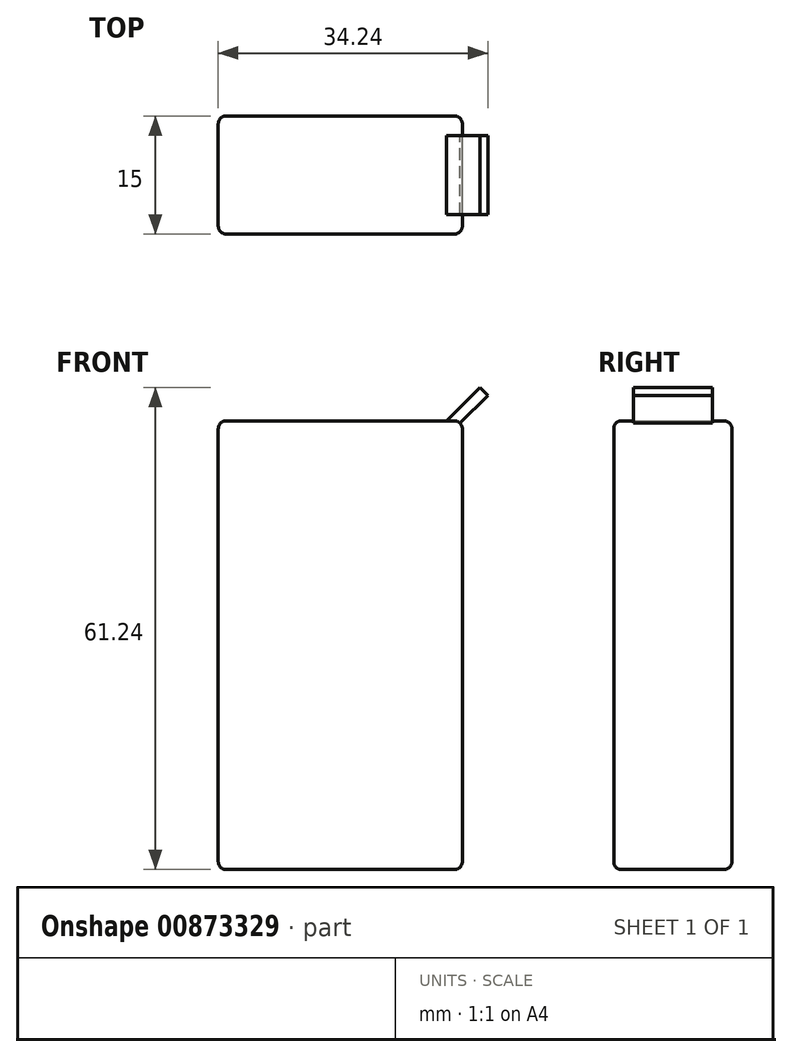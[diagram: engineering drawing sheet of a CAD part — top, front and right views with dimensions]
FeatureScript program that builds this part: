
annotation { "Feature Type Name" : "Feature", "Feature Type Description" : "" }
export const myFeature = defineFeature(function(context is Context, id is Id, definition is map)
    precondition{}
    {
        {
            var Q0;
            Q0=qCreatedBy(makeId("Front.planeOp"),FACE);
            var sketch = newSketch(context, id + "F0", { "sketchPlane" : qUnion([Q0])});
            skLineSegment(sketch, "E0.bottom", {"start": v(1, 0) * mm, "end": v(30, 0) * mm});
            skLineSegment(sketch, "E0.top", {"start": v(1, -57) * mm, "end": v(30, -57) * mm});
            skLineSegment(sketch, "E0.left", {"start": v(0, -1) * mm, "end": v(0, -56) * mm});
            skLineSegment(sketch, "E0.right", {"start": v(31, -1) * mm, "end": v(31, -56) * mm});
            skPoint(sketch, "E1.visualSharp", {"position": v(31, 0) * mm});
            skArc(sketch, "E1.filletArc", {"start": v(31, -1) * mm, "mid": v(30.7, -0.3) * mm, "end": v(30, 0) * mm});
            skPoint(sketch, "E2.visualSharp", {"position": v(31, -57) * mm});
            skArc(sketch, "E2.filletArc", {"start": v(30, -57) * mm, "mid": v(30.7, -56.7) * mm, "end": v(31, -56) * mm});
            skPoint(sketch, "E3.visualSharp", {"position": v(0, -57) * mm});
            skArc(sketch, "E3.filletArc", {"start": v(0, -56) * mm, "mid": v(0.3, -56.7) * mm, "end": v(1, -57) * mm});
            skPoint(sketch, "E4.visualSharp", {"position": v(0, 0) * mm});
            skArc(sketch, "E4.filletArc", {"start": v(1, 0) * mm, "mid": v(0.3, -0.3) * mm, "end": v(0, -1) * mm});
            skSolve(sketch);
        }
        {
            var Q0;
            Q0=makeQuery(id+"F0.imprint","IMPRINT",FACE,{"disambiguationData":[TD([[makeQuery(id+"F0.imprint","IMPRINT",EDGE,{"derivedFrom":sQuery(id+"F0.wireOp",EDGE,"E0.bottom")}),-1.0]])]});
            extrude(context, id + "F1", {"entities" : qUnion([Q0]), "endBound" : BoundingType.SYMMETRIC, "depth" : 15 * mm, "offsetDistance" : 25 * mm});
        }
        {
            var Q0;
            Q0=makeQuery(id+"F1.opExtrude","CAP_FACE",FACE,{"disambiguationData":[OSD([sQuery(id+"F0.wireOp",EDGE,"E0.bottom"),sQuery(id+"F0.wireOp",EDGE,"E0.top"),sQuery(id+"F0.wireOp",EDGE,"E0.left"),sQuery(id+"F0.wireOp",EDGE,"E0.right"),sQuery(id+"F0.wireOp",EDGE,"E1.filletArc"),sQuery(id+"F0.wireOp",EDGE,"E2.filletArc"),sQuery(id+"F0.wireOp",EDGE,"E3.filletArc"),sQuery(id+"F0.wireOp",EDGE,"E4.filletArc")])],"isStart":false});
            var Q1;
            Q1=makeQuery(id+"F1.opExtrude","CAP_FACE",FACE,{"disambiguationData":[OSD([sQuery(id+"F0.wireOp",EDGE,"E0.bottom"),sQuery(id+"F0.wireOp",EDGE,"E0.top"),sQuery(id+"F0.wireOp",EDGE,"E0.left"),sQuery(id+"F0.wireOp",EDGE,"E0.right"),sQuery(id+"F0.wireOp",EDGE,"E1.filletArc"),sQuery(id+"F0.wireOp",EDGE,"E2.filletArc"),sQuery(id+"F0.wireOp",EDGE,"E3.filletArc"),sQuery(id+"F0.wireOp",EDGE,"E4.filletArc")])],"isStart":true});
            fillet(context, id + "F2", {"entities" : qUnion([Q0, Q1]), "radius" : 1 * mm, "tangentPropagation" : true, "allowEdgeOverflow" : false});
        }
        {
            var Q0;
            Q0=qCreatedBy(makeId("Front.planeOp"),FACE);
            var sketch = newSketch(context, id + "F3", { "sketchPlane" : qUnion([Q0])});
            skPoint(sketch, "E5", {"position": v(30, -1) * mm});
            skLineSegment(sketch, "E6", {"start": v(30, -1) * mm, "end": v(34.24, 3.24) * mm});
            skLineSegment(sketch, "E7", {"start": v(34.24, 3.24) * mm, "end": v(33.24, 4.24) * mm});
            skLineSegment(sketch, "E8", {"start": v(33.24, 4.24) * mm, "end": v(29, 0) * mm});
            skLineSegment(sketch, "E9", {"start": v(29, 0) * mm, "end": v(30, -1) * mm});
            skSolve(sketch);
        }
        {
            var Q0;
            Q0=makeQuery(id+"F3.imprint","IMPRINT",FACE,{"disambiguationData":[TD([[makeQuery(id+"F3.imprint","IMPRINT",EDGE,{"derivedFrom":sQuery(id+"F3.wireOp",EDGE,"E6")}),1.0]])]});
            extrude(context, id + "F4", {"entities" : qUnion([Q0]), "operationType" : NewBodyOperationType.ADD, "endBound" : BoundingType.SYMMETRIC, "depth" : 10 * mm, "offsetDistance" : 25 * mm});
        }
    });
